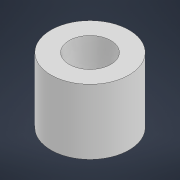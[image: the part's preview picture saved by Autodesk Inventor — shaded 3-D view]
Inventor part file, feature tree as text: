
AUTODESK INVENTOR PART (.ipt)
format: ipt  version: 2021 (Build 250183000, 183)  size: 205,824 bytes
history: native  units: mm
features: extrude x1, sketch x1
ambient origin geometry x8: Origin, YZ Plane, XZ Plane, XY Plane, X Axis, Y Axis, Z Axis, Center Point
bodies: Volumenkörper1 (feature_tree)
feature tree (2):
  extrude  "Extrusion1"  Depth=5.0mm
  sketch  "Skizze1"  dims[d0=3.2mm d1=6.0mm d2=5.0mm d3=0.0mm]
